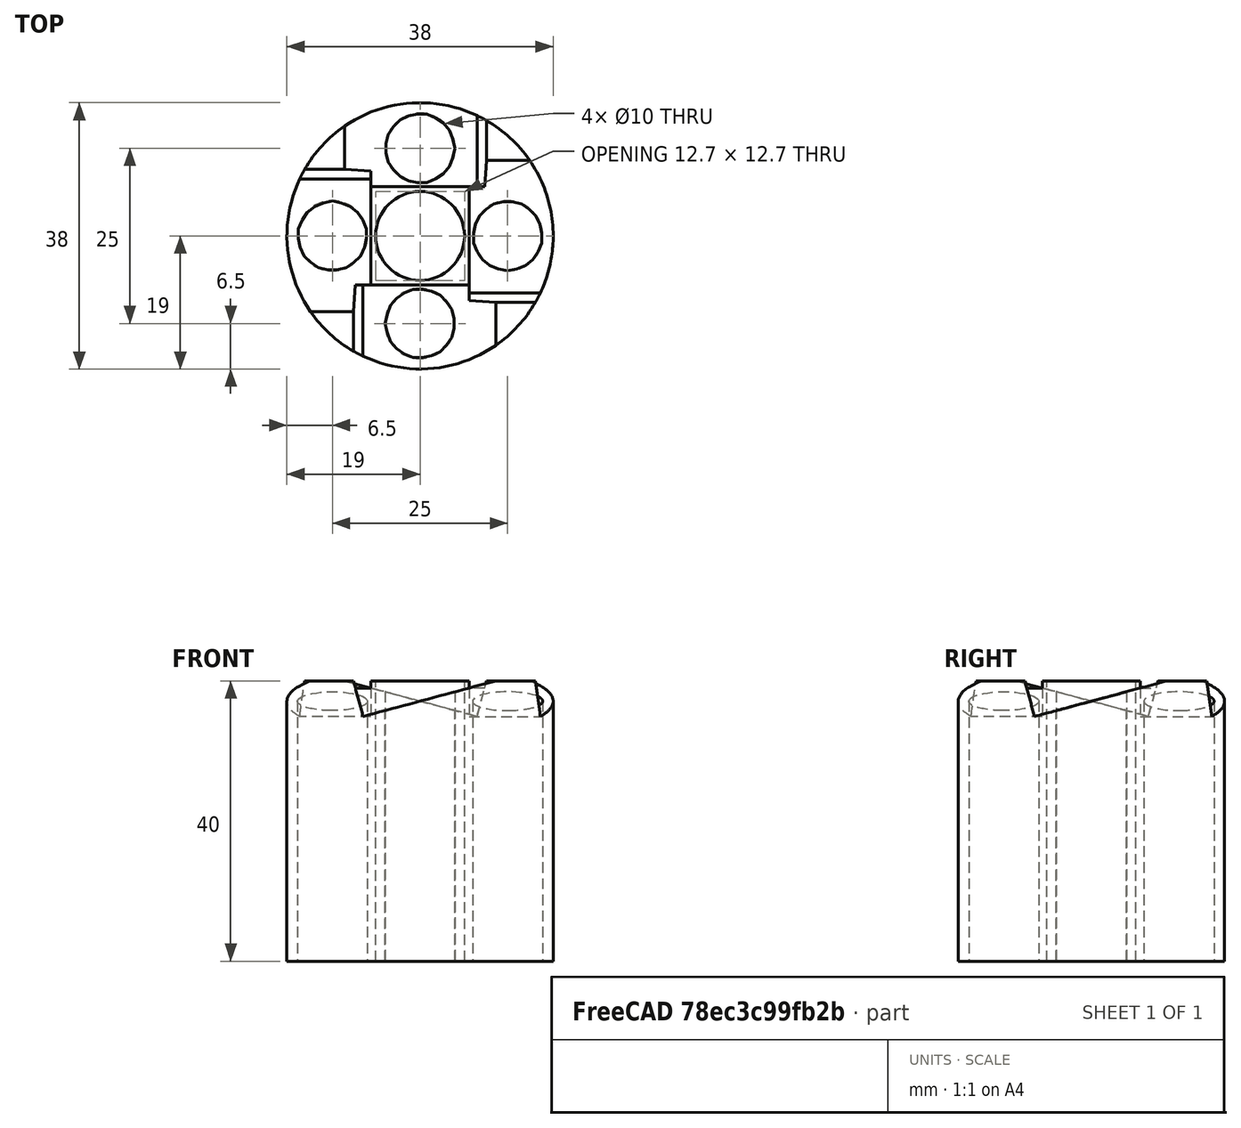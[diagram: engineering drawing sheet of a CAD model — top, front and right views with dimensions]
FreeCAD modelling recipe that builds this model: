
FCSTD DOCUMENT  (FreeCAD 0.20R29410 (Git))
Label: cylinderFour0
License: All rights reserved
LicenseURL: http://en.wikipedia.org/wiki/All_rights_reserved
objects: Part::MultiFuse×11, Part::Cylinder×10, Part::Box×4, Part::Cut×2, Part::Feature×1
note: 28 computed .brp shape members not serialized (recipe doc carries the construction recipe); baked Part::Feature solids carry a one-line shape summary decoded from their .brp

FEATURE [Part::Cylinder] Cylinder
  Angle = 360
  AttacherType = Attacher::AttachEngine3D
  FirstAngle = 0
  Height = 40
  Radius = 19
  SecondAngle = 0
FEATURE [Part::Cylinder] Cylinder001
  Angle = 360
  AttacherType = Attacher::AttachEngine3D
  FirstAngle = 0
  Height = 50
  Placement = pos=(0,12.5,0) rot=(0,0,1;0rad)
  Radius = 5
  SecondAngle = 0
FEATURE [Part::Cylinder] Cylinder003  label="bevilPin"
  Angle = 360
  AttacherType = Attacher::AttachEngine3D
  FirstAngle = 0
  Height = 50
  Radius = 6.35
  SecondAngle = 0
FEATURE [Part::Cylinder] Cylinder004  label="bevilPin001"
  Angle = 360
  AttacherType = Attacher::AttachEngine3D
  FirstAngle = 0
  Height = 50
  Radius = 6.35
  SecondAngle = 0
FEATURE [Part::Box] Box  label="Cube"
  AttacherType = Attacher::AttachEngine3D
  Height = 30
  Length = 20
  Placement = pos=(-11.1838,7,40.104) rot=(0,1,0;0.261799rad)
  Width = 20
FEATURE [Part::MultiFuse] Fusion
  Shapes = -> [Cylinder001,Box]
FEATURE [Part::MultiFuse] Fusion001
  Shapes = -> [Fusion,Cylinder004]
FEATURE [Part::Box] Box001  label="Cube001"
  AttacherType = Attacher::AttachEngine3D
  Height = 30
  Length = 20
  Placement = pos=(-11.1838,7,40.104) rot=(0,1,0;0.261799rad)
  Width = 20
FEATURE [Part::Cylinder] Cylinder005
  Angle = 360
  AttacherType = Attacher::AttachEngine3D
  FirstAngle = 0
  Height = 50
  Placement = pos=(0,12.5,0) rot=(0,0,1;0rad)
  Radius = 5
  SecondAngle = 0
FEATURE [Part::Cylinder] Cylinder006  label="bevilPin002"
  Angle = 360
  AttacherType = Attacher::AttachEngine3D
  FirstAngle = 0
  Height = 50
  Radius = 6.35
  SecondAngle = 0
FEATURE [Part::MultiFuse] Fusion002
  Shapes = -> [Cylinder005,Box001]
FEATURE [Part::MultiFuse] Fusion003
  Placement = pos=(0,0,0) rot=(0,0,1;3.14159rad)
  Shapes = -> [Fusion002,Cylinder006]
FEATURE [Part::MultiFuse] Fusion004
  Shapes = -> [Fusion003,Fusion001]
FEATURE [Part::Box] Box002  label="Cube002"
  AttacherType = Attacher::AttachEngine3D
  Height = 30
  Length = 20
  Placement = pos=(-11.1838,7,40.104) rot=(0,1,0;0.261799rad)
  Width = 20
FEATURE [Part::Box] Box003  label="Cube003"
  AttacherType = Attacher::AttachEngine3D
  Height = 30
  Length = 20
  Placement = pos=(-11.1838,7,40.104) rot=(0,1,0;0.261799rad)
  Width = 20
FEATURE [Part::Cylinder] Cylinder007
  Angle = 360
  AttacherType = Attacher::AttachEngine3D
  FirstAngle = 0
  Height = 50
  Placement = pos=(0,12.5,0) rot=(0,0,1;0rad)
  Radius = 5
  SecondAngle = 0
FEATURE [Part::Cylinder] Cylinder008  label="bevilPin003"
  Angle = 360
  AttacherType = Attacher::AttachEngine3D
  FirstAngle = 0
  Height = 50
  Radius = 6.35
  SecondAngle = 0
FEATURE [Part::Cylinder] Cylinder009
  Angle = 360
  AttacherType = Attacher::AttachEngine3D
  FirstAngle = 0
  Height = 50
  Placement = pos=(0,12.5,0) rot=(0,0,1;0rad)
  Radius = 5
  SecondAngle = 0
FEATURE [Part::Cylinder] Cylinder010  label="bevilPin004"
  Angle = 360
  AttacherType = Attacher::AttachEngine3D
  FirstAngle = 0
  Height = 50
  Radius = 6.35
  SecondAngle = 0
FEATURE [Part::MultiFuse] Fusion005
  Shapes = -> [Cylinder007,Box002]
FEATURE [Part::MultiFuse] Fusion006
  Shapes = -> [Fusion005,Cylinder008]
FEATURE [Part::MultiFuse] Fusion007
  Shapes = -> [Cylinder009,Box003]
FEATURE [Part::MultiFuse] Fusion008
  Placement = pos=(0,0,0) rot=(0,0,1;3.14159rad)
  Shapes = -> [Fusion007,Cylinder010]
FEATURE [Part::MultiFuse] Fusion009
  Placement = pos=(0,0,0) rot=(0,0,1;4.71239rad)
  Shapes = -> [Fusion008,Fusion006]
FEATURE [Part::MultiFuse] Fusion010
  Shapes = -> [Fusion009,Fusion004]
FEATURE [Part::Cut] Cut
  Base = -> Cylinder
  Tool = -> Fusion010
FEATURE [Part::Cut] Cut001
  Base = -> Cut
  Tool = -> Cylinder003
FEATURE [Part::Feature] Cut001_solid  label="Cut001 (Solid)"
  shape: bbox 38 x 38 x 40 mm, 27 faces (baked)
